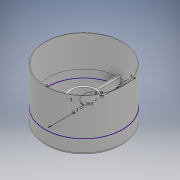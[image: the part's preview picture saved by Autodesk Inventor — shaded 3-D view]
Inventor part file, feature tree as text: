
AUTODESK INVENTOR PART (.ipt)
format: ipt  version: 2018 (Build 220112000, 112)  size: 248,320 bytes
history: native  units: mm
features: fillet x5, extrude x3, sketch x1, chamfer x1
ambient origin geometry x8: Origin, YZ Plane, XZ Plane, XY Plane, X Axis, Y Axis, Z Axis, Center Point
bodies: Solid1 (feature_tree)
feature tree (10):
  sketch  "Sketch1"  dims[d0=24.5mm d1=77.0mm d2=3.0mm d3=3.0mm d4=3.0mm d6=3.0mm d7=180.0deg d8=10.0mm d9=0.0mm d10=15.0mm d11=0.0mm d12=2.0mm d13=40.0mm d14=0.0mm d16=2.0mm d17=1.0mm d18=1.0mm d19=1.0mm d20=2.5mm d21=2.0mm d22=14.922565mm]
  extrude  "Extrusion1"  Depth=1.0mm
  extrude  "Extrusion2"  Depth=1.0mm
  fillet  "Fillet1"  Radius=3.0mm
  extrude  "Extrusion3"  Depth=1.0mm
  fillet  "Fillet3"  Radius=3.0mm
  fillet  "Fillet4"  [1 undecoded]
  fillet  "Fillet5"  Radius=10.0mm
  fillet  "Fillet6"  Radius=15.0mm
  chamfer  "Chamfer1"  Distance=2.0mm
note: 1 required parameter value undecoded (feature->parameter linkage not recoverable at this tier; creation-order binding heuristic only, values carry confidence <= 0.55)
